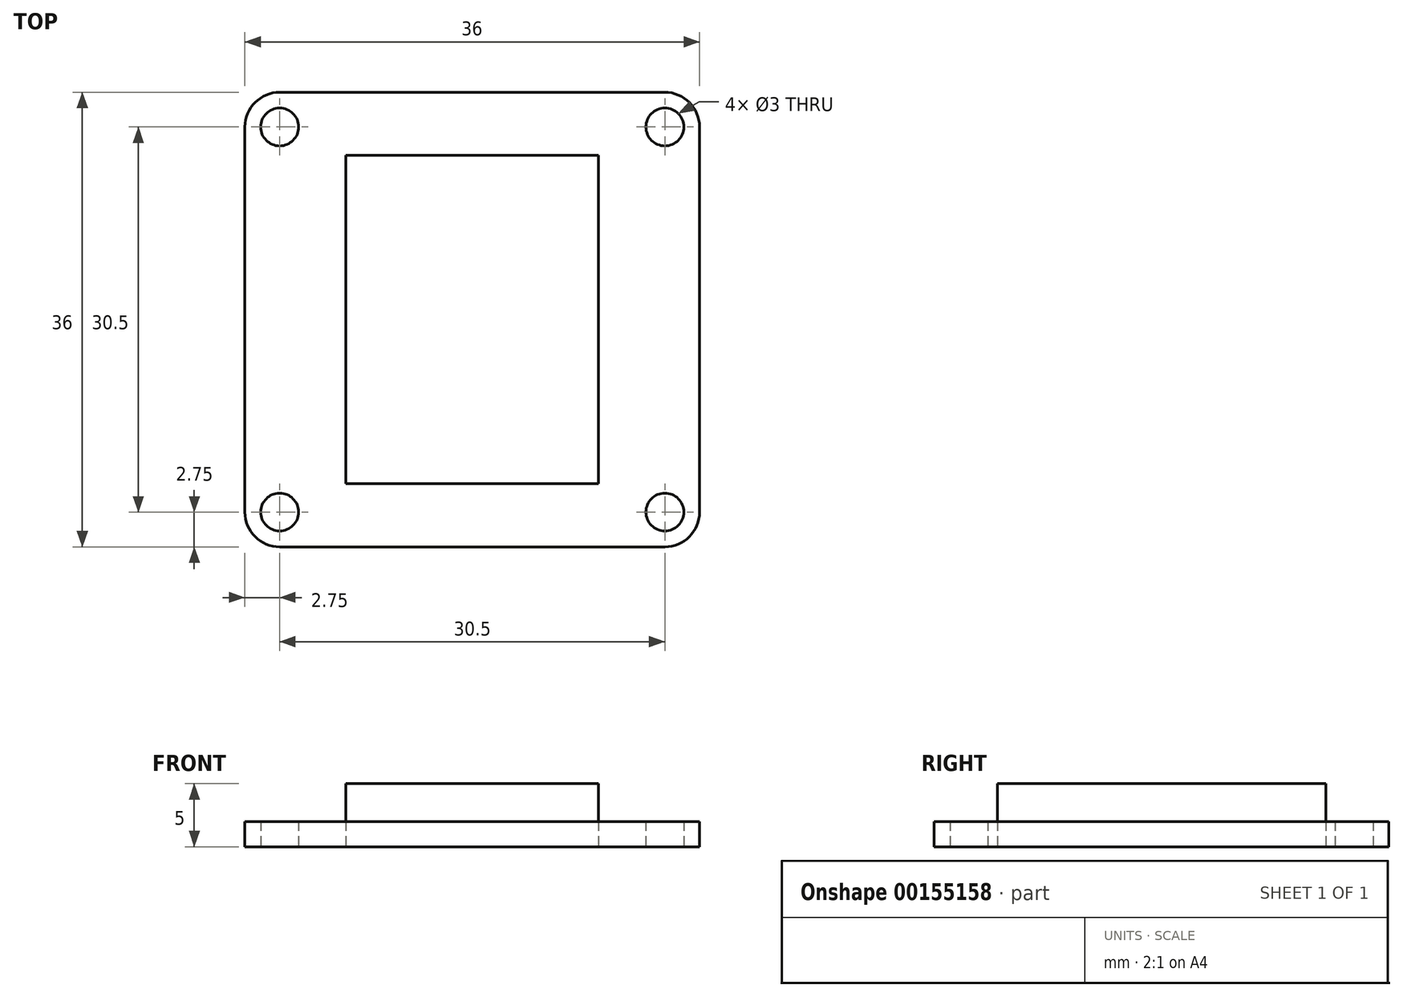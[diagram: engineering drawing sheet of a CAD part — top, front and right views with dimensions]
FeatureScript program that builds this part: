
annotation { "Feature Type Name" : "Feature", "Feature Type Description" : "" }
export const myFeature = defineFeature(function(context is Context, id is Id, definition is map)
    precondition{}
    {
        {
            var Q0;
            Q0=qCreatedBy(makeId("Top.planeOp"),FACE);
            var sketch = newSketch(context, id + "F0", { "sketchPlane" : qUnion([Q0])});
            skLineSegment(sketch, "E0.bottom", {"start": v(-15.25, 18) * mm, "end": v(15.25, 18) * mm});
            skLineSegment(sketch, "E0.top", {"start": v(-15.25, -18) * mm, "end": v(15.25, -18) * mm});
            skLineSegment(sketch, "E0.left", {"start": v(-18, 15.25) * mm, "end": v(-18, -15.25) * mm});
            skLineSegment(sketch, "E0.right", {"start": v(18, 15.25) * mm, "end": v(18, -15.25) * mm});
            skCircle(sketch, "E1", {"center": v(-15.25, 15.25) * mm, "radius": 1.5 * mm});
            skCircle(sketch, "E2.0.1.0", {"center": v(-15.25, -15.25) * mm, "radius": 1.5 * mm});
            skCircle(sketch, "E2.1.0.0", {"center": v(15.25, 15.25) * mm, "radius": 1.5 * mm});
            skCircle(sketch, "E2.1.1.0", {"center": v(15.25, -15.25) * mm, "radius": 1.5 * mm});
            skLineSegment(sketch, "E2.direction1", {"start": v(-15.25, 15.25) * mm, "end": v(15.25, 15.25) * mm, "construction": true});
            skLineSegment(sketch, "E2.direction2", {"start": v(-15.25, 15.25) * mm, "end": v(-15.25, -15.25) * mm, "construction": true});
            skPoint(sketch, "E3.visualSharp", {"position": v(-18, 18) * mm});
            skArc(sketch, "E3.filletArc", {"start": v(-15.25, 18) * mm, "mid": v(-17.2, 17.2) * mm, "end": v(-18, 15.25) * mm});
            skPoint(sketch, "E4.visualSharp", {"position": v(18, 18) * mm});
            skArc(sketch, "E4.filletArc", {"start": v(18, 15.25) * mm, "mid": v(17.2, 17.2) * mm, "end": v(15.25, 18) * mm});
            skPoint(sketch, "E5.visualSharp", {"position": v(18, -18) * mm});
            skArc(sketch, "E5.filletArc", {"start": v(15.25, -18) * mm, "mid": v(17.2, -17.2) * mm, "end": v(18, -15.25) * mm});
            skPoint(sketch, "E6.visualSharp", {"position": v(-18, -18) * mm});
            skArc(sketch, "E6.filletArc", {"start": v(-18, -15.25) * mm, "mid": v(-17.2, -17.2) * mm, "end": v(-15.25, -18) * mm});
            skSolve(sketch);
        }
        {
            var Q0;
            Q0=makeQuery(id+"F0.imprint","IMPRINT",FACE,{"disambiguationData":[TD([[makeQuery(id+"F0.imprint","IMPRINT",EDGE,{"derivedFrom":sQuery(id+"F0.wireOp",EDGE,"E0.bottom")}),-1.0]])]});
            extrude(context, id + "F1", {"entities" : qUnion([Q0]), "depth" : 2 * mm});
        }
        {
            var Q0;
            Q0=qCreatedBy(makeId("Top.planeOp"),FACE);
            var sketch = newSketch(context, id + "F2", { "sketchPlane" : qUnion([Q0])});
            skLineSegment(sketch, "E7.bottom", {"start": v(-10, 13) * mm, "end": v(10, 13) * mm});
            skLineSegment(sketch, "E7.top", {"start": v(-10, -13) * mm, "end": v(10, -13) * mm});
            skLineSegment(sketch, "E7.left", {"start": v(-10, 13) * mm, "end": v(-10, -13) * mm});
            skLineSegment(sketch, "E7.right", {"start": v(10, 13) * mm, "end": v(10, -13) * mm});
            skSolve(sketch);
        }
        {
            var Q0;
            Q0 = qSketchRegion(id + "F2", true);
            extrude(context, id + "F3", {"entities" : qUnion([Q0]), "depth" : 5 * mm});
        }
    });
